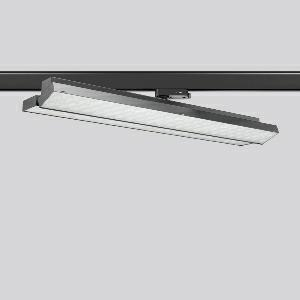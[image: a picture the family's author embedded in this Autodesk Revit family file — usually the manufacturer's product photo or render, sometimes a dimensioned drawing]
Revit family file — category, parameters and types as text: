
# Revit family: tx-move_742162_003_3_1217
name_source: partatom
category: Lighting Fixtures
units: mm (PartAtom-declared; Revit-internal decimal feet)

## family parameters
Cut with Voids When Loaded = No
Host = Face
Light Source = No
Part Type = Normal
Room Calculation Point = No
Round Connector Dimension = Use Diameter
Shared = No

## types (1)
- MultiLumen 1 (1 x LED Modul 835, 3050 lm, 3500)
    Apparent Load = 41 VA
    CIE Flux Codes = 77 96 99 100 100
    Color Rendering = 80
    Color Temperature = 3500
    Default Elevation = 1800 mm
    Description = Series: TX-MOVE
Multifunctional surface-mounted spotlight for area lighting. Very flat design. Housing: sheet steel, powder-coated. Rotation range: 356°. Swivel range: 90°. Consistent alignment possible with visible tilt scale. High-efficiency LED units with optimum light control thanks to clear plastic (PC) lens optics. Spezielle Mikrostrukturen reduzieren Gelbsaum. Symmetrical light distribution. With multi adaptor for 3-circuit tracks 230 V. Suitable for Track on ceiling. MultiLumen: Luminous flux adjustable in 3 steps. Factory setting is the highest luminous flux. Environmentally friendly and resource-saving due to replaceable and recyclable components. 
Colour: deep black, matt (RAL 9005)
Length: 570 mm
Width: 119 mm
Height: 92 mm
Lamp: LED
Socket: without socket
Colour temperature: 3500K
Colour rendering index (CRI): 80
System power: 41 W
Rated luminous flux: 6100 lm
Luminous efficiency: 149 lm/W
System power 2: 57 W
Rated luminous flux 2: 8300 lm
Luminous efficiency 2: 146 lm/W
System power 3: 73 W
Rated luminous flux 3: 10200 lm
Luminous efficiency 3: 140 lm/W
Control gear: Regulated power supply
Protection class: I
Type of protection: IP 20
    Height = 75 mm
    Lamp = 1 x LED Modul 835
    Lamp Light Flux = 3050 lm
    Lamp count = 1
    Length = 569 mm
    Lifetime = 50000 h
    Luminous efficacy = 149 lm/W
    Manufacturer = RZB
    ModVariant = No
    Model = 742162.003.3
    Mounting Place = Ceiling
    Mounting Type = Rail mounted
    Number of Poles = 1
    OnlyDefault = Yes
    Power Factor = 1
    Product Name = TX-MOVE
    Product group = Track mounted projectors
    ProductGroupID = 301
    Protection Class = Protection class I
    Protection Degree = IP 20
    RLX_Detail_Level = 1
    RLX_Emergency_Light_Flux = 0 lm
    RLX_Emergency_Type = 0
    RLX_Emergency_Type_DB = No
    RlxData = <blob elided: 36725 chars, md5=522fe5eb>
    Socket = socket
    Standby Power = 0 W
    System Light Flux = 6100 lm
    System Power = 41 W
    Type Comments = MultiLumen 1
    Type Image = 742162.003.jpg
    URL = http://relux.com
    VarID = multilumen_1
    Voltage = 230 V
    Voltage Range = 220-240 V
    Weight = 0.00 kg
    Width = 119 mm

## geometry (parser evidence)
native form markers: Blend x4, Sweep x16
no freeform markers — native parametric forms only
